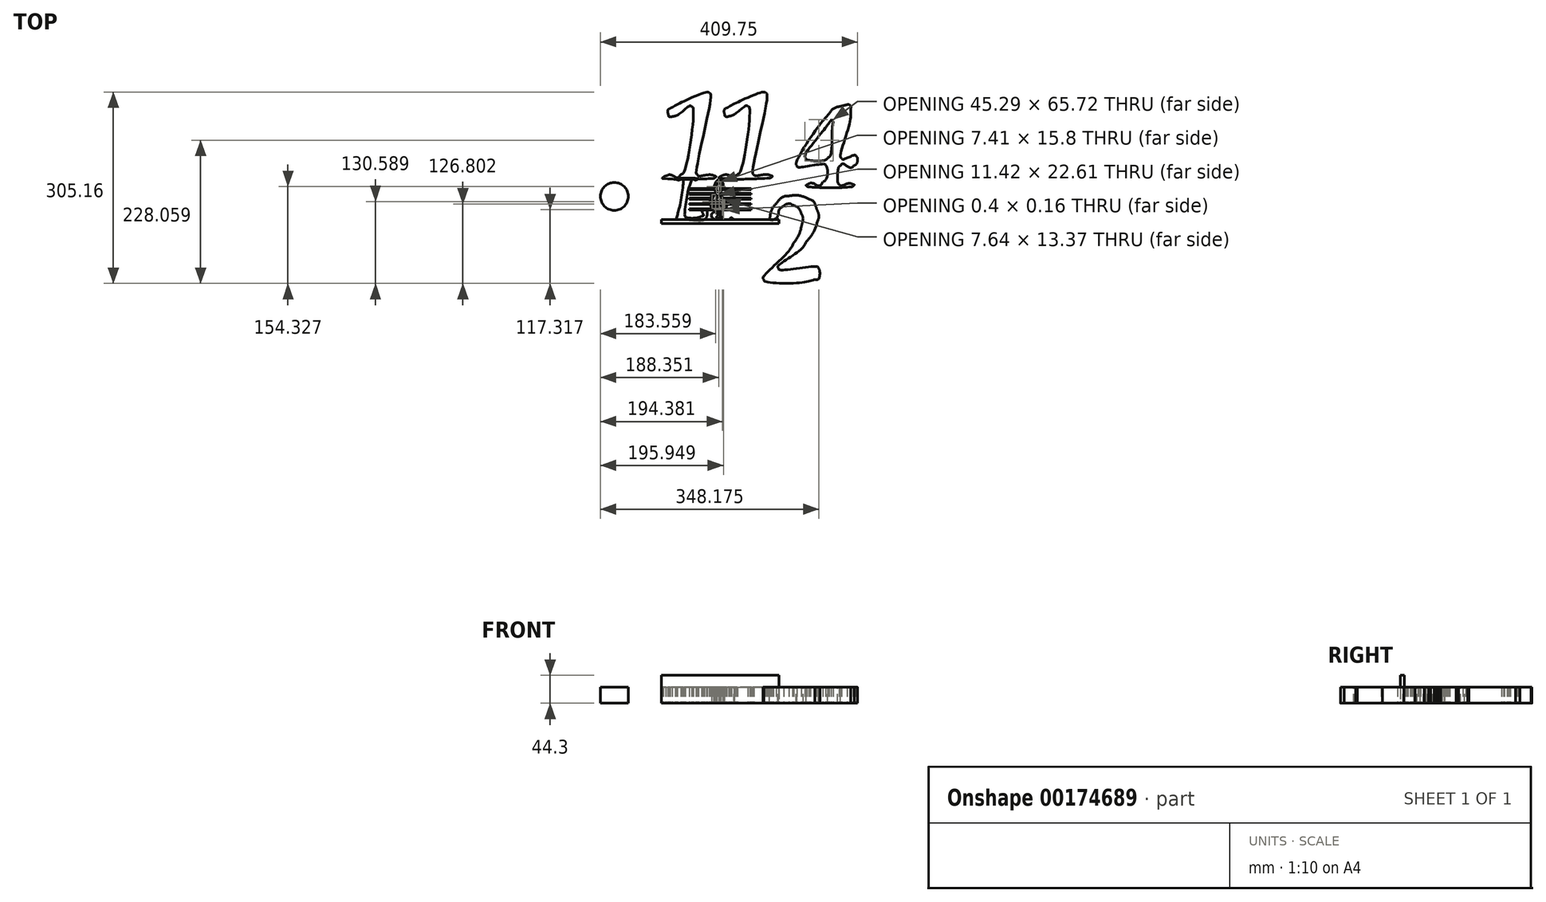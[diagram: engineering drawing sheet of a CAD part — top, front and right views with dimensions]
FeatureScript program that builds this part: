
annotation { "Feature Type Name" : "Feature", "Feature Type Description" : "" }
export const myFeature = defineFeature(function(context is Context, id is Id, definition is map)
    precondition{}
    {
        {
            var Q0;
            Q0=qCreatedBy(makeId("Top.planeOp"),FACE);
            var sketch = newSketch(context, id + "F0", { "sketchPlane" : qUnion([Q0])});
            skFitSpline(sketch, "E0", {"points": [v(-67.19, 65.64) * mm, v(-68.14, 65.58) * mm, v(-66.1, 63.8) * mm, v(-65.16, 63.61) * mm]});
            skFitSpline(sketch, "E1", {"points": [v(-65.16, 63.61) * mm, v(-62.39, 63.08) * mm, v(-57.66, 64.74) * mm, v(-56.7, 63.61) * mm]});
            skFitSpline(sketch, "E2", {"points": [v(-56.7, 63.61) * mm, v(-55.74, 62.49) * mm, v(-61.1, 22.51) * mm, v(-66.5, 2.65) * mm]});
            skFitSpline(sketch, "E3", {"points": [v(-66.5, 2.65) * mm, v(-67.1, 0.47) * mm, v(-71.2, 3.54) * mm, v(-73.28, 2.65) * mm]});
            skFitSpline(sketch, "E4", {"points": [v(-73.28, 2.65) * mm, v(-74.16, 2.28) * mm, v(-72.2, 0.66) * mm, v(-71.25, 0.62) * mm]});
            skFitSpline(sketch, "E5", {"points": [v(-71.25, 0.62) * mm, v(-54.74, -0.03) * mm, v(-24.37, -1.55) * mm, v(-21.68, 0.62) * mm]});
            skFitSpline(sketch, "E6", {"points": [v(-21.68, 0.62) * mm, v(-19, 2.8) * mm, v(-17.38, 14.81) * mm, v(-18.42, 15.86) * mm]});
            skFitSpline(sketch, "E7", {"points": [v(-18.42, 15.86) * mm, v(-19.46, 16.91) * mm, v(-22.45, 16.22) * mm, v(-23.5, 14.84) * mm]});
            skFitSpline(sketch, "E8", {"points": [v(-23.5, 14.84) * mm, v(-25.4, 12.34) * mm, v(-23.13, 6.82) * mm, v(-26.1, 5.76) * mm]});
            skFitSpline(sketch, "E9", {"points": [v(-26.1, 5.76) * mm, v(-34.27, 2.85) * mm, v(-51.14, 3.53) * mm, v(-52.12, 4.63) * mm]});
            skFitSpline(sketch, "E10", {"points": [v(-52.12, 4.63) * mm, v(-53.1, 5.74) * mm, v(-48.12, 44.5) * mm, v(-42.47, 63.61) * mm]});
            skFitSpline(sketch, "E11", {"points": [v(-42.47, 63.61) * mm, v(-41.73, 66.1) * mm, v(-37.22, 63.09) * mm, v(-34.68, 63.61) * mm]});
            skFitSpline(sketch, "E12", {"points": [v(-34.68, 63.61) * mm, v(-33.74, 63.8) * mm, v(-31.69, 65.58) * mm, v(-32.64, 65.64) * mm]});
            skFitSpline(sketch, "E13", {"points": [v(-32.64, 65.64) * mm, v(-44.14, 66.36) * mm, v(-55.7, 66.36) * mm, v(-67.19, 65.64) * mm]});
            skFitSpline(sketch, "E14", {"points": [v(26.27, 65.22) * mm, v(25.32, 65.16) * mm, v(27.37, 63.37) * mm, v(28.3, 63.19) * mm]});
            skFitSpline(sketch, "E15", {"points": [v(28.3, 63.19) * mm, v(31.07, 62.65) * mm, v(35.8, 64.31) * mm, v(36.76, 63.19) * mm]});
            skFitSpline(sketch, "E16", {"points": [v(36.76, 63.19) * mm, v(37.72, 62.07) * mm, v(32.67, 22) * mm, v(26.96, 2.23) * mm]});
            skFitSpline(sketch, "E17", {"points": [v(26.96, 2.23) * mm, v(26.24, -0.27) * mm, v(21.62, 3.1) * mm, v(19.16, 2.23) * mm]});
            skFitSpline(sketch, "E18", {"points": [v(19.16, 2.23) * mm, v(18.26, 1.91) * mm, v(20.24, 0.23) * mm, v(21.2, 0.2) * mm]});
            skFitSpline(sketch, "E19", {"points": [v(21.2, 0.2) * mm, v(38.04, -0.45) * mm, v(69.09, -1.98) * mm, v(71.78, 0.2) * mm]});
            skFitSpline(sketch, "E20", {"points": [v(71.78, 0.2) * mm, v(74.47, 2.37) * mm, v(76.08, 14.39) * mm, v(75.04, 15.44) * mm]});
            skFitSpline(sketch, "E21", {"points": [v(75.04, 15.44) * mm, v(74, 16.49) * mm, v(71, 15.8) * mm, v(69.96, 14.42) * mm]});
            skFitSpline(sketch, "E22", {"points": [v(69.96, 14.42) * mm, v(68.06, 11.91) * mm, v(70.33, 6.4) * mm, v(67.37, 5.34) * mm]});
            skFitSpline(sketch, "E23", {"points": [v(67.37, 5.34) * mm, v(59.19, 2.42) * mm, v(42.32, 3.1) * mm, v(41.34, 4.2) * mm]});
            skFitSpline(sketch, "E24", {"points": [v(41.34, 4.2) * mm, v(40.36, 5.31) * mm, v(45.34, 44.09) * mm, v(51, 63.19) * mm]});
            skFitSpline(sketch, "E25", {"points": [v(51, 63.19) * mm, v(51.73, 65.68) * mm, v(56.24, 62.66) * mm, v(58.79, 63.19) * mm]});
            skFitSpline(sketch, "E26", {"points": [v(58.79, 63.19) * mm, v(59.72, 63.38) * mm, v(61.77, 65.16) * mm, v(60.82, 65.22) * mm]});
            skFitSpline(sketch, "E27", {"points": [v(60.82, 65.22) * mm, v(49.33, 65.94) * mm, v(37.77, 65.94) * mm, v(26.27, 65.22) * mm]});
            skFitSpline(sketch, "E28", {"points": [v(-21.1, 68.31) * mm, v(-18.95, 68.64) * mm, v(-16.7, 68.16) * mm, v(-14.64, 67.5) * mm]});
            skFitSpline(sketch, "E29", {"points": [v(-14.64, 67.5) * mm, v(-12.7, 66.88) * mm, v(-10.84, 65.85) * mm, v(-9.27, 64.55) * mm]});
            skFitSpline(sketch, "E30", {"points": [v(-9.27, 64.55) * mm, v(-7.12, 62.77) * mm, v(-5.25, 60.63) * mm, v(-3.62, 58.37) * mm]});
            skFitSpline(sketch, "E31", {"points": [v(-3.62, 58.37) * mm, v(-2.27, 56.48) * mm, v(-0.79, 52.19) * mm, v(-0.4, 52.18) * mm]});
            skFitSpline(sketch, "E32", {"points": [v(-0.4, 52.18) * mm, v(0, 52.18) * mm, v(2.03, 57.19) * mm, v(3.64, 59.44) * mm]});
            skFitSpline(sketch, "E33", {"points": [v(3.64, 59.44) * mm, v(4.92, 61.25) * mm, v(6.51, 62.84) * mm, v(8.2, 64.28) * mm]});
            skFitSpline(sketch, "E34", {"points": [v(8.2, 64.28) * mm, v(9.5, 65.37) * mm, v(10.95, 66.32) * mm, v(12.5, 66.97) * mm]});
            skFitSpline(sketch, "E35", {"points": [v(12.5, 66.97) * mm, v(14.21, 67.68) * mm, v(16.04, 68.17) * mm, v(17.88, 68.31) * mm]});
            skFitSpline(sketch, "E36", {"points": [v(17.88, 68.31) * mm, v(21.33, 68.58) * mm, v(25.13, 67.5) * mm, v(27.83, 65.35) * mm]});
            skFitSpline(sketch, "E37", {"points": [v(27.83, 65.35) * mm, v(29.52, 64.01) * mm, v(31.1, 62.41) * mm, v(32.13, 60.52) * mm]});
            skFitSpline(sketch, "E38", {"points": [v(32.13, 60.52) * mm, v(33.57, 57.85) * mm, v(34.71, 54.92) * mm, v(35.09, 51.91) * mm]});
            skFitSpline(sketch, "E39", {"points": [v(35.09, 51.91) * mm, v(35.86, 45.7) * mm, v(34.5, 39.2) * mm, v(32.13, 33.37) * mm]});
            skFitSpline(sketch, "E40", {"points": [v(32.13, 33.37) * mm, v(31, 30.58) * mm, v(29.63, 27.89) * mm, v(28.1, 25.3) * mm]});
            skFitSpline(sketch, "E41", {"points": [v(28.1, 25.3) * mm, v(26.76, 23.03) * mm, v(25.23, 20.86) * mm, v(23.53, 18.85) * mm]});
            skFitSpline(sketch, "E42", {"points": [v(23.53, 18.85) * mm, v(21.2, 16.1) * mm, v(18.67, 13.48) * mm, v(16, 11.05) * mm]});
            skFitSpline(sketch, "E43", {"points": [v(16, 11.05) * mm, v(13.73, 9) * mm, v(11.3, 7.1) * mm, v(8.74, 5.4) * mm]});
            skFitSpline(sketch, "E44", {"points": [v(8.74, 5.4) * mm, v(5.9, 3.52) * mm, v(1.61, 0.32) * mm, v(-0.13, 0.3) * mm]});
            skFitSpline(sketch, "E45", {"points": [v(-0.13, 0.3) * mm, v(-1.87, 0.29) * mm, v(-7.2, 3.64) * mm, v(-10.34, 5.95) * mm]});
            skFitSpline(sketch, "E46", {"points": [v(-10.34, 5.95) * mm, v(-14.69, 9.14) * mm, v(-18.7, 12.8) * mm, v(-22.44, 16.7) * mm]});
            skFitSpline(sketch, "E47", {"points": [v(-22.44, 16.7) * mm, v(-24.92, 19.29) * mm, v(-27.1, 22.2) * mm, v(-28.9, 25.3) * mm]});
            skFitSpline(sketch, "E48", {"points": [v(-28.9, 25.3) * mm, v(-31.06, 29.05) * mm, v(-32.8, 33.06) * mm, v(-34.27, 37.13) * mm]});
            skFitSpline(sketch, "E49", {"points": [v(-34.27, 37.13) * mm, v(-35.14, 39.54) * mm, v(-35.6, 42.1) * mm, v(-35.88, 44.66) * mm]});
            skFitSpline(sketch, "E50", {"points": [v(-35.88, 44.66) * mm, v(-36.35, 48.86) * mm, v(-36.04, 53.38) * mm, v(-34.54, 57.3) * mm]});
            skFitSpline(sketch, "E51", {"points": [v(-34.54, 57.3) * mm, v(-33.87, 59.01) * mm, v(-32.94, 60.64) * mm, v(-31.85, 62.13) * mm]});
            skFitSpline(sketch, "E52", {"points": [v(-31.85, 62.13) * mm, v(-30.95, 63.36) * mm, v(-29.94, 64.6) * mm, v(-28.62, 65.35) * mm]});
            skFitSpline(sketch, "E53", {"points": [v(-28.62, 65.35) * mm, v(-26.28, 66.7) * mm, v(-23.76, 67.9) * mm, v(-21.1, 68.31) * mm]});
            skPoint(sketch, "E54", {"position": v(-0.13, 0.3) * mm});
            skSolve(sketch);
        }
        {
            var Q0;
            Q0=qCreatedBy(makeId("Top.planeOp"),FACE);
            var sketch = newSketch(context, id + "F1", { "sketchPlane" : qUnion([Q0])});
            skFitSpline(sketch, "E55", {"points": [v(-13.96, 201.4) * mm, v(-16.25, 203.24) * mm, v(-56.77, 187.9) * mm, v(-76.45, 177.37) * mm]});
            skFitSpline(sketch, "E56", {"points": [v(-76.45, 177.37) * mm, v(-79.73, 175.62) * mm, v(-80.1, 170.16) * mm, v(-79.16, 166.56) * mm]});
            skFitSpline(sketch, "E57", {"points": [v(-79.16, 166.56) * mm, v(-78.62, 164.5) * mm, v(-75.1, 163.82) * mm, v(-73.1, 164.55) * mm]});
            skFitSpline(sketch, "E58", {"points": [v(-73.1, 164.55) * mm, v(-62.33, 168.46) * mm, v(-44.7, 181.66) * mm, v(-42.34, 179.93) * mm]});
            skFitSpline(sketch, "E59", {"points": [v(-42.34, 179.93) * mm, v(-39.98, 178.2) * mm, v(-53.95, 77.46) * mm, v(-59.58, 72.15) * mm]});
            skFitSpline(sketch, "E60", {"points": [v(-59.58, 72.15) * mm, v(-65.22, 66.84) * mm, v(-75.48, 71.57) * mm, v(-83.19, 69.79) * mm]});
            skFitSpline(sketch, "E61", {"points": [v(-83.19, 69.79) * mm, v(-85.04, 69.36) * mm, v(-89.12, 65.86) * mm, v(-87.22, 65.76) * mm]});
            skFitSpline(sketch, "E62", {"points": [v(-87.22, 65.76) * mm, v(-61.05, 64.34) * mm, v(-34.77, 64.58) * mm, v(-8.6, 65.76) * mm]});
            skFitSpline(sketch, "E63", {"points": [v(-8.6, 65.76) * mm, v(-6.85, 65.83) * mm, v(-3.2, 69.02) * mm, v(-4.9, 69.45) * mm]});
            skFitSpline(sketch, "E64", {"points": [v(-4.9, 69.45) * mm, v(-14.03, 71.79) * mm, v(-31.24, 69.71) * mm, v(-33.05, 72.01) * mm]});
            skFitSpline(sketch, "E65", {"points": [v(-33.05, 72.01) * mm, v(-34.86, 74.31) * mm, v(-11.68, 199.58) * mm, v(-13.96, 201.4) * mm]});
            skFitSpline(sketch, "E66", {"points": [v(75.76, 201.83) * mm, v(73.47, 203.66) * mm, v(32.95, 188.31) * mm, v(13.26, 177.8) * mm]});
            skFitSpline(sketch, "E67", {"points": [v(13.26, 177.8) * mm, v(9.99, 176.04) * mm, v(9.62, 170.58) * mm, v(10.56, 166.98) * mm]});
            skFitSpline(sketch, "E68", {"points": [v(10.56, 166.98) * mm, v(11.1, 164.93) * mm, v(14.61, 164.24) * mm, v(16.6, 164.97) * mm]});
            skFitSpline(sketch, "E69", {"points": [v(16.6, 164.97) * mm, v(27.39, 168.88) * mm, v(45.02, 182.08) * mm, v(47.38, 180.35) * mm]});
            skFitSpline(sketch, "E70", {"points": [v(47.38, 180.35) * mm, v(49.74, 178.62) * mm, v(35.77, 77.88) * mm, v(30.13, 72.57) * mm]});
            skFitSpline(sketch, "E71", {"points": [v(30.13, 72.57) * mm, v(24.5, 67.26) * mm, v(14.23, 72) * mm, v(6.53, 70.2) * mm]});
            skFitSpline(sketch, "E72", {"points": [v(6.53, 70.2) * mm, v(4.68, 69.78) * mm, v(0.6, 66.28) * mm, v(2.5, 66.18) * mm]});
            skFitSpline(sketch, "E73", {"points": [v(2.5, 66.18) * mm, v(28.67, 64.76) * mm, v(54.94, 65) * mm, v(81.13, 66.18) * mm]});
            skFitSpline(sketch, "E74", {"points": [v(81.13, 66.18) * mm, v(82.87, 66.25) * mm, v(86.5, 69.44) * mm, v(84.82, 69.87) * mm]});
            skFitSpline(sketch, "E75", {"points": [v(84.82, 69.87) * mm, v(75.7, 72.2) * mm, v(58.48, 70.13) * mm, v(56.66, 72.43) * mm]});
            skFitSpline(sketch, "E76", {"points": [v(56.66, 72.43) * mm, v(54.85, 74.73) * mm, v(78.04, 200) * mm, v(75.76, 201.83) * mm]});
            skFitSpline(sketch, "E77", {"points": [v(205.18, 183.26) * mm, v(207.95, 183.9) * mm, v(211.5, 180.05) * mm, v(211.22, 177.2) * mm]});
            skFitSpline(sketch, "E78", {"points": [v(211.22, 177.2) * mm, v(208.57, 150.6) * mm, v(194.7, 100.45) * mm, v(196.69, 98.3) * mm]});
            skFitSpline(sketch, "E79", {"points": [v(196.69, 98.3) * mm, v(198.68, 96.17) * mm, v(217.94, 103.09) * mm, v(219.86, 100.88) * mm]});
            skFitSpline(sketch, "E80", {"points": [v(219.86, 100.88) * mm, v(221.8, 98.68) * mm, v(220.54, 88.98) * mm, v(216.26, 86.48) * mm]});
            skFitSpline(sketch, "E81", {"points": [v(216.26, 86.48) * mm, v(210.22, 82.95) * mm, v(198.45, 89.44) * mm, v(195.25, 86.48) * mm]});
            skFitSpline(sketch, "E82", {"points": [v(195.25, 86.48) * mm, v(192.05, 83.52) * mm, v(190.93, 58.39) * mm, v(192.92, 56.24) * mm]});
            skFitSpline(sketch, "E83", {"points": [v(192.92, 56.24) * mm, v(194.91, 54.1) * mm, v(207.99, 57.84) * mm, v(215.26, 56.24) * mm]});
            skFitSpline(sketch, "E84", {"points": [v(215.26, 56.24) * mm, v(217.11, 55.83) * mm, v(213.12, 52.32) * mm, v(211.22, 52.2) * mm]});
            skFitSpline(sketch, "E85", {"points": [v(211.22, 52.2) * mm, v(189.08, 50.94) * mm, v(166.84, 51.13) * mm, v(144.7, 52.2) * mm]});
            skFitSpline(sketch, "E86", {"points": [v(144.7, 52.2) * mm, v(143.09, 52.29) * mm, v(139.77, 55.07) * mm, v(141.28, 55.62) * mm]});
            skFitSpline(sketch, "E87", {"points": [v(141.28, 55.62) * mm, v(149.43, 58.58) * mm, v(160.83, 54.05) * mm, v(166.87, 60.27) * mm]});
            skFitSpline(sketch, "E88", {"points": [v(166.87, 60.27) * mm, v(173.04, 66.63) * mm, v(173.13, 84.25) * mm, v(171.24, 86.48) * mm]});
            skFitSpline(sketch, "E89", {"points": [v(171.24, 86.48) * mm, v(169.35, 88.72) * mm, v(126.7, 83.92) * mm, v(125.29, 86.48) * mm]});
            skFitSpline(sketch, "E90", {"points": [v(125.29, 86.48) * mm, v(123.87, 89.04) * mm, v(156.26, 144.09) * mm, v(176.95, 169.14) * mm]});
            skFitSpline(sketch, "E91", {"points": [v(176.95, 169.14) * mm, v(183.65, 177.26) * mm, v(194.94, 180.85) * mm, v(205.18, 183.26) * mm]});
            skFitSpline(sketch, "E92", {"points": [v(179.78, 158.25) * mm, v(180.7, 159.45) * mm, v(183.13, 156.54) * mm, v(183, 155.03) * mm]});
            skFitSpline(sketch, "E93", {"points": [v(183, 155.03) * mm, v(181.36, 136.08) * mm, v(178.93, 102.28) * mm, v(174.64, 98.58) * mm]});
            skFitSpline(sketch, "E94", {"points": [v(174.64, 98.58) * mm, v(170.34, 94.88) * mm, v(140.66, 96) * mm, v(139.3, 98.58) * mm]});
            skFitSpline(sketch, "E95", {"points": [v(139.3, 98.58) * mm, v(137.92, 101.17) * mm, v(165.07, 139.24) * mm, v(179.78, 158.25) * mm]});
            skCircle(sketch, "E96", {"center": v(-165.43, 37.15) * mm, "radius": 22.2 * mm});
            skCircle(sketch, "E97", {"center": v(-179.1, -33.64) * mm, "radius": 24.93 * mm});
            skFitSpline(sketch, "E98", {"points": [v(-168.77, 68.16) * mm, v(-157.86, 69) * mm, v(-145.47, 68.38) * mm, v(-136.51, 62.1) * mm]});
            skFitSpline(sketch, "E99", {"points": [v(-136.51, 62.1) * mm, v(-130.07, 57.6) * mm, v(-128.88, 47.79) * mm, v(-128.45, 39.93) * mm]});
            skFitSpline(sketch, "E100", {"points": [v(-128.45, 39.93) * mm, v(-128.16, 34.82) * mm, v(-131.13, 29.67) * mm, v(-134.5, 25.82) * mm]});
            skFitSpline(sketch, "E101", {"points": [v(-134.5, 25.82) * mm, v(-140.79, 18.63) * mm, v(-156.7, 10.6) * mm, v(-156.67, 7.67) * mm]});
            skFitSpline(sketch, "E102", {"points": [v(-156.67, 7.67) * mm, v(-156.64, 4.75) * mm, v(-142.22, 0.28) * mm, v(-138.53, -6.44) * mm]});
            skFitSpline(sketch, "E103", {"points": [v(-138.53, -6.44) * mm, v(-134.27, -14.18) * mm, v(-132.35, -24.07) * mm, v(-134.5, -32.65) * mm]});
            skFitSpline(sketch, "E104", {"points": [v(-134.5, -32.65) * mm, v(-136.71, -41.52) * mm, v(-143.66, -48.9) * mm, v(-150.63, -54.83) * mm]});
            skFitSpline(sketch, "E105", {"points": [v(-150.63, -54.83) * mm, v(-157.5, -60.66) * mm, v(-165.9, -65.6) * mm, v(-174.82, -66.92) * mm]});
            skFitSpline(sketch, "E106", {"points": [v(-174.82, -66.92) * mm, v(-184.88, -68.41) * mm, v(-195.46, -66.25) * mm, v(-205.06, -62.9) * mm]});
            skFitSpline(sketch, "E107", {"points": [v(-205.06, -62.9) * mm, v(-209.55, -61.32) * mm, v(-213.56, -57.3) * mm, v(-215.14, -52.8) * mm]});
            skFitSpline(sketch, "E108", {"points": [v(-215.14, -52.8) * mm, v(-217.83, -45.18) * mm, v(-221, -35.74) * mm, v(-217.16, -28.62) * mm]});
            skFitSpline(sketch, "E109", {"points": [v(-217.16, -28.62) * mm, v(-210.62, -16.47) * mm, v(-186.97, -3.32) * mm, v(-186.92, -0.4) * mm]});
            skFitSpline(sketch, "E110", {"points": [v(-186.92, -0.4) * mm, v(-186.86, 2.54) * mm, v(-200.22, 8.68) * mm, v(-203.04, 15.74) * mm]});
            skFitSpline(sketch, "E111", {"points": [v(-203.04, 15.74) * mm, v(-206.04, 23.23) * mm, v(-205.6, 32.28) * mm, v(-203.04, 39.93) * mm]});
            skFitSpline(sketch, "E112", {"points": [v(-203.04, 39.93) * mm, v(-200.62, 47.2) * mm, v(-194.85, 53.2) * mm, v(-188.93, 58.08) * mm]});
            skFitSpline(sketch, "E113", {"points": [v(-188.93, 58.08) * mm, v(-183.13, 62.85) * mm, v(-176.26, 67.58) * mm, v(-168.77, 68.16) * mm]});
            skFitSpline(sketch, "E114", {"points": [v(112.48, 37.8) * mm, v(124, 39.09) * mm, v(136.2, 36.56) * mm, v(146.75, 31.76) * mm]});
            skFitSpline(sketch, "E115", {"points": [v(146.75, 31.76) * mm, v(152.01, 29.37) * mm, v(154.8, 23.06) * mm, v(156.83, 17.65) * mm]});
            skFitSpline(sketch, "E116", {"points": [v(156.83, 17.65) * mm, v(158.97, 11.95) * mm, v(160.64, 5.32) * mm, v(158.85, -0.5) * mm]});
            skFitSpline(sketch, "E117", {"points": [v(158.85, -0.5) * mm, v(155.05, -12.85) * mm, v(148.88, -24.76) * mm, v(140.7, -34.77) * mm]});
            skFitSpline(sketch, "E118", {"points": [v(140.7, -34.77) * mm, v(127.76, -50.62) * mm, v(95.16, -74.4) * mm, v(96.25, -77.11) * mm]});
            skFitSpline(sketch, "E119", {"points": [v(96.25, -77.11) * mm, v(97.34, -79.83) * mm, v(157.66, -74.77) * mm, v(159.42, -77.11) * mm]});
            skFitSpline(sketch, "E120", {"points": [v(159.42, -77.11) * mm, v(161.19, -79.45) * mm, v(160.4, -93.97) * mm, v(154.24, -95.26) * mm]});
            skFitSpline(sketch, "E121", {"points": [v(154.24, -95.26) * mm, v(127.57, -100.82) * mm, v(73.77, -97.9) * mm, v(72.52, -95.26) * mm]});
            skFitSpline(sketch, "E122", {"points": [v(72.52, -95.26) * mm, v(71.26, -92.6) * mm, v(105.94, -57.35) * mm, v(120.54, -36.79) * mm]});
            skFitSpline(sketch, "E123", {"points": [v(120.54, -36.79) * mm, v(126.11, -28.94) * mm, v(130.21, -19.89) * mm, v(132.64, -10.58) * mm]});
            skFitSpline(sketch, "E124", {"points": [v(132.64, -10.58) * mm, v(134.34, -4.08) * mm, v(135.2, 3.37) * mm, v(132.64, 9.58) * mm]});
            skFitSpline(sketch, "E125", {"points": [v(132.64, 9.58) * mm, v(130.1, 15.73) * mm, v(124.64, 21.07) * mm, v(118.53, 23.7) * mm]});
            skFitSpline(sketch, "E126", {"points": [v(118.53, 23.7) * mm, v(114.16, 25.57) * mm, v(108.12, 24.65) * mm, v(104.41, 21.68) * mm]});
            skFitSpline(sketch, "E127", {"points": [v(104.41, 21.68) * mm, v(97.28, 15.97) * mm, v(95.05, 5.65) * mm, v(88.28, -0.5) * mm]});
            skFitSpline(sketch, "E128", {"points": [v(88.28, -0.5) * mm, v(86.71, -1.93) * mm, v(81.91, -0.58) * mm, v(82.24, 1.52) * mm]});
            skFitSpline(sketch, "E129", {"points": [v(82.24, 1.52) * mm, v(83.56, 10.15) * mm, v(86.72, 19) * mm, v(92.32, 25.71) * mm]});
            skFitSpline(sketch, "E130", {"points": [v(92.32, 25.71) * mm, v(97.33, 31.73) * mm, v(104.69, 36.94) * mm, v(112.48, 37.8) * mm]});
            skSolve(sketch);
        }
        {
            var Q0;
            Q0=qCreatedBy(makeId("Front.planeOp"),FACE);
            var sketch = newSketch(context, id + "F2", { "sketchPlane" : qUnion([Q0])});
            skLineSegment(sketch, "E131.bottom", {"start": v(-90.24, 44.3) * mm, "end": v(96.59, 44.3) * mm});
            skLineSegment(sketch, "E131.top", {"start": v(-90.24, 0) * mm, "end": v(96.59, 0) * mm});
            skLineSegment(sketch, "E131.left", {"start": v(-90.24, 44.3) * mm, "end": v(-90.24, 0) * mm});
            skLineSegment(sketch, "E131.right", {"start": v(96.59, 44.3) * mm, "end": v(96.59, 0) * mm});
            skSolve(sketch);
        }
        {
            var Q0;
            Q0=qCreatedBy(makeId("Top.planeOp"),FACE);
            var sketch = newSketch(context, id + "F3", { "sketchPlane" : qUnion([Q0])});
            skFitSpline(sketch, "E132", {"points": [v(-5.3, 47.83) * mm, v(-5.86, 54.73) * mm, v(0.98, 64.25) * mm, v(7.14, 59.17) * mm, v(5.66, 46.69) * mm, v(0, 41.97) * mm], "startDerivative": vector(-5.6, 41.47) * mm, "endDerivative": vector(-39.7, -43.44) * mm});
            skFitSpline(sketch, "E133", {"points": [v(0, 60.06) * mm, v(-2.64, 55.14) * mm, v(-2.9, 49.86) * mm, v(-1.46, 44.95) * mm, v(2.21, 47.64) * mm, v(4.41, 52.36) * mm, v(3.06, 60.64) * mm, v(0, 60.06) * mm]});
            skFitSpline(sketch, "E134", {"points": [v(-5.3, 47.83) * mm, v(-5.3, 43.19) * mm, v(-10.5, 37.81) * mm, v(-12.78, 25.6) * mm, v(-7.85, 15.62) * mm, v(1.82, 14.54) * mm], "startDerivative": vector(32.53, -78.9) * mm, "endDerivative": vector(54.35, 5.43) * mm});
            skFitSpline(sketch, "E135", {"points": [v(-5.6, 38.99) * mm, v(-7.33, 37.3) * mm, v(-9.74, 28.78) * mm, v(-5.98, 19.06) * mm, v(1.6, 18.11) * mm, v(1.43, 19.35) * mm, v(-0.79, 30.61) * mm, v(-3, 29.17) * mm, v(-3.77, 25.51) * mm, v(-2.04, 23.2) * mm, v(-1.56, 20.8) * mm, v(-5.07, 22.67) * mm, v(-5.6, 29.84) * mm, v(-1.65, 34.37) * mm, v(-1.65, 35.62) * mm, v(-2.69, 39.1) * mm, v(-3.2, 40.43) * mm, v(-5.6, 38.99) * mm]});
            skFitSpline(sketch, "E136", {"points": [v(0, 41.97) * mm, v(2.3, 35.59) * mm, v(5.8, 36.08) * mm, v(12.46, 30.82) * mm, v(12.88, 19.68) * mm, v(8.53, 15.92) * mm, v(7.62, 15.66) * mm], "startDerivative": vector(7.56, -39.68) * mm, "endDerivative": vector(-6.64, 1.58) * mm});
            skFitSpline(sketch, "E137", {"points": [v(3.45, 31.57) * mm, v(3.06, 28.5) * mm, v(5.09, 18.87) * mm, v(8.17, 19.83) * mm, v(10.56, 24.3) * mm, v(7.69, 31.25) * mm, v(3.45, 31.57) * mm]});
            skFitSpline(sketch, "E138", {"points": [v(1.82, 14.54) * mm, v(2.47, 10.16) * mm, v(2.87, 3.85) * mm, v(0, 2.7) * mm, v(-3.2, 2.8) * mm, v(-3.2, 3.76) * mm, v(-1.62, 5.08) * mm, v(-0.2, 7.82) * mm, v(-1.84, 10.87) * mm, v(-5.62, 12.24) * mm, v(-9.83, 9.78) * mm, v(-10.86, 6.25) * mm, v(-9.97, 3.87) * mm, v(-6.59, 0.95) * mm, v(0.95, 0) * mm, v(4.5, 1.35) * mm, v(6.34, 5.28) * mm, v(5.44, 14.54) * mm, v(7.77, 15.62) * mm, v(8.53, 15.92) * mm], "startDerivative": vector(8.69, -71.8) * mm, "endDerivative": vector(18.16, 2.08) * mm});
            skPoint(sketch, "E139", {"position": v(-3.85, 32.12) * mm});
            skLineSegment(sketch, "E140.bottom", {"start": v(-45.75, 49.51) * mm, "end": v(52.46, 49.51) * mm});
            skLineSegment(sketch, "E140.top", {"start": v(-45.75, 47.83) * mm, "end": v(52.46, 47.83) * mm});
            skLineSegment(sketch, "E140.left", {"start": v(-45.75, 49.51) * mm, "end": v(-45.75, 47.83) * mm});
            skLineSegment(sketch, "E140.right", {"start": v(52.46, 49.51) * mm, "end": v(52.46, 47.83) * mm});
            skLineSegment(sketch, "E141.bottom", {"start": v(-45.78, 42.21) * mm, "end": v(52.43, 42.21) * mm});
            skLineSegment(sketch, "E141.top", {"start": v(-45.78, 40.53) * mm, "end": v(52.43, 40.53) * mm});
            skLineSegment(sketch, "E141.left", {"start": v(-45.78, 42.21) * mm, "end": v(-45.78, 40.53) * mm});
            skLineSegment(sketch, "E141.right", {"start": v(52.43, 42.21) * mm, "end": v(52.43, 40.53) * mm});
            skLineSegment(sketch, "E142.bottom", {"start": v(-45.8, 34.62) * mm, "end": v(52.42, 34.62) * mm});
            skLineSegment(sketch, "E142.top", {"start": v(-45.8, 32.94) * mm, "end": v(52.42, 32.94) * mm});
            skLineSegment(sketch, "E142.left", {"start": v(-45.8, 34.62) * mm, "end": v(-45.8, 32.94) * mm});
            skLineSegment(sketch, "E142.right", {"start": v(52.42, 34.62) * mm, "end": v(52.42, 32.94) * mm});
            skLineSegment(sketch, "E143.bottom", {"start": v(-45.8, 25.9) * mm, "end": v(52.42, 25.9) * mm});
            skLineSegment(sketch, "E143.top", {"start": v(-45.8, 24.22) * mm, "end": v(52.42, 24.22) * mm});
            skLineSegment(sketch, "E143.left", {"start": v(-45.8, 25.9) * mm, "end": v(-45.8, 24.22) * mm});
            skLineSegment(sketch, "E143.right", {"start": v(52.42, 25.9) * mm, "end": v(52.42, 24.22) * mm});
            skLineSegment(sketch, "E144.bottom", {"start": v(-45.85, 17.43) * mm, "end": v(52.36, 17.43) * mm});
            skLineSegment(sketch, "E144.top", {"start": v(-45.85, 15.75) * mm, "end": v(52.36, 15.75) * mm});
            skLineSegment(sketch, "E144.left", {"start": v(-45.85, 17.43) * mm, "end": v(-45.85, 15.75) * mm});
            skLineSegment(sketch, "E144.right", {"start": v(52.36, 17.43) * mm, "end": v(52.36, 15.75) * mm});
            skSolve(sketch);
        }
        {
            var Q0;
            Q0=makeQuery(id+"F0.imprint","IMPRINT",FACE,{"disambiguationData":[TD([[makeQuery(id+"F0.imprint","IMPRINT",EDGE,{"derivedFrom":sQuery(id+"F0.wireOp",EDGE,"E0")}),1.0]])]});
            var Q1;
            {var subQ10=sQuery(id+"F0.wireOp",EDGE,"E17");Q1=makeQuery(id+"F0.imprint","IMPRINT",FACE,{"disambiguationData":[TD([[makeQuery(id+"F0.imprint","IMPRINT",EDGE,{"derivedFrom":subQ10}),1.0]])]});}
            var Q2;
            {var subQ0=sQuery(id+"F0.wireOp",EDGE,"E14");Q2=makeQuery(id+"F0.imprint","IMPRINT",FACE,{"disambiguationData":[TD([[makeQuery(id+"F0.imprint","IMPRINT",EDGE,{"derivedFrom":subQ0}),1.0]])]});}
            var Q3;
            {var subQ0=sQuery(id+"F0.wireOp",EDGE,"E7");var subQ1=sQuery(id+"F0.wireOp",EDGE,"E6");var subQ2=makeQuery(id+"F0.imprint","INTERSECT",VERTEX,{"derivedFrom":[subQ1,subQ0]});Q3=makeQuery(id+"F0.imprint","IMPRINT",FACE,{"disambiguationData":[TD([[makeQuery(id+"F0.imprint","IMPRINT",EDGE,{"disambiguationData":[TD([[subQ2,1.0]])],"derivedFrom":subQ1}),1.0]])]});}
            extrude(context, id + "F4", {"entities" : qUnion([Q0, Q1, Q2, Q3]), "depth" : 25.4 * mm});
        }
        {
            var Q0;
            Q0=makeQuery(id+"F1.imprint","IMPRINT",FACE,{"disambiguationData":[TD([[makeQuery(id+"F1.imprint","IMPRINT",EDGE,{"derivedFrom":sQuery(id+"F1.wireOp",EDGE,"E55")}),1.0]])]});
            var Q1;
            Q1=makeQuery(id+"F1.imprint","IMPRINT",FACE,{"disambiguationData":[TD([[makeQuery(id+"F1.imprint","IMPRINT",EDGE,{"derivedFrom":sQuery(id+"F1.wireOp",EDGE,"E66")}),1.0]])]});
            var Q2;
            Q2=makeQuery(id+"F1.imprint","IMPRINT",FACE,{"disambiguationData":[TD([[makeQuery(id+"F1.imprint","IMPRINT",EDGE,{"derivedFrom":sQuery(id+"F1.wireOp",EDGE,"E77")}),-1.0]])]});
            var Q3;
            Q3=makeQuery(id+"F1.imprint","IMPRINT",FACE,{"disambiguationData":[TD([[makeQuery(id+"F1.imprint","IMPRINT",EDGE,{"derivedFrom":sQuery(id+"F1.wireOp",EDGE,"E96")}),1.0]])]});
            var Q4;
            Q4=makeQuery(id+"F1.imprint","IMPRINT",FACE,{"disambiguationData":[TD([[makeQuery(id+"F1.imprint","IMPRINT",EDGE,{"derivedFrom":sQuery(id+"F1.wireOp",EDGE,"E114")}),-1.0]])]});
            var Q5;
            Q5=sQuery(id+"F1.wireOp",EDGE,"c7cc00ab-f25f-42a7-9330-9939b61b4846");
            var Q6;
            Q6=sQuery(id+"F1.wireOp",EDGE,"f25bb9a9-3208-4804-8311-45a919a4e9d7");
            var Q7;
            Q7=sQuery(id+"F1.wireOp",EDGE,"843194b1-cb39-4e59-84b3-f443d2b2ed2d");
            var Q8;
            Q8=sQuery(id+"F1.wireOp",EDGE,"fd73b015-e9e2-47a3-8cee-78b48e1bb1c8");
            var Q9;
            Q9=sQuery(id+"F1.wireOp",EDGE,"1f206ff0-db46-4620-826d-d70bbf3d78a3");
            var Q10;
            Q10=sQuery(id+"F1.wireOp",EDGE,"01695f1d-dff9-4f9b-8fe2-ccf91e0bb2d9");
            var Q11;
            Q11=sQuery(id+"F1.wireOp",EDGE,"32f496c9-434c-4a42-a456-453a450ef25a");
            var Q12;
            Q12=sQuery(id+"F1.wireOp",EDGE,"f1e4f423-0778-4f18-887f-b8ced6975a27");
            var Q13;
            Q13=sQuery(id+"F1.wireOp",EDGE,"50f9aca0-c4ca-4987-b3e7-d789c735e512");
            var Q14;
            Q14=sQuery(id+"F1.wireOp",EDGE,"892d63bd-c6f6-4b77-9e03-ff4d23a4ebc5");
            var Q15;
            Q15=sQuery(id+"F1.wireOp",EDGE,"9eea7301-c211-4749-b727-e29ea0ed2ce4");
            var Q16;
            Q16=sQuery(id+"F1.wireOp",EDGE,"90398055-b3c3-411f-ad3e-85c2e70ec0a7");
            var Q17;
            Q17=sQuery(id+"F1.wireOp",EDGE,"6a25daee-9104-4236-8762-4ed708dfe10a");
            var Q18;
            Q18=sQuery(id+"F1.wireOp",EDGE,"9c4817a0-864d-4a76-afd6-0ea0e7f3b45a");
            var Q19;
            Q19=sQuery(id+"F1.wireOp",EDGE,"6609a38f-e891-4cee-82b8-8241b089ebb5");
            var Q20;
            Q20=sQuery(id+"F1.wireOp",EDGE,"e3be049d-917c-41fb-82a8-84bd116318f2");
            var Q21;
            Q21=sQuery(id+"F1.wireOp",EDGE,"39e6c882-b98c-4de5-8e09-77840ac4508f");
            extrude(context, id + "F5", {"entities" : qUnion([Q0, Q1, Q2, Q3, Q4]), "surfaceEntities" : qUnion([Q5, Q6, Q7, Q8, Q9, Q10, Q11, Q12, Q13, Q14, Q15, Q16, Q17, Q18, Q19, Q20, Q21]), "depth" : 25.4 * mm});
        }
        {
            var Q0;
            Q0=makeQuery(id+"F2.imprint","IMPRINT",FACE,{"disambiguationData":[TD([[makeQuery(id+"F2.imprint","IMPRINT",EDGE,{"derivedFrom":sQuery(id+"F2.wireOp",EDGE,"E131.bottom")}),-1.0]])]});
            extrude(context, id + "F6", {"entities" : qUnion([Q0]), "depth" : 6.35 * mm});
        }
        {
            var Q0;
            Q0 = qSketchRegion(id + "F3", true);
            var Q1;
            {var subQ0=sQuery(id+"F3.wireOp",EDGE,"E143.top");var subQ1=sQuery(id+"F3.wireOp",EDGE,"E135");var subQ2=makeQuery(id+"F3.imprint","INTERSECT",VERTEX,{"disambiguationData":[OD(2.0)],"derivedFrom":[subQ1,subQ0]});Q1=makeQuery(id+"F3.imprint","IMPRINT",FACE,{"disambiguationData":[TD([[makeQuery(id+"F3.imprint","IMPRINT",EDGE,{"disambiguationData":[TD([[subQ2,-1.0]])],"derivedFrom":subQ1}),-1.0]])]});}
            var Q2;
            {var subQ0=sQuery(id+"F3.wireOp",EDGE,"E143.bottom");var subQ1=sQuery(id+"F3.wireOp",EDGE,"E135");var subQ2=makeQuery(id+"F3.imprint","INTERSECT",VERTEX,{"disambiguationData":[OD(2.0)],"derivedFrom":[subQ1,subQ0]});Q2=makeQuery(id+"F3.imprint","IMPRINT",FACE,{"disambiguationData":[TD([[makeQuery(id+"F3.imprint","IMPRINT",EDGE,{"disambiguationData":[TD([[subQ2,-1.0]])],"derivedFrom":subQ1}),-1.0]])]});}
            var Q3;
            {var subQ0=sQuery(id+"F3.wireOp",EDGE,"E143.top");var subQ1=sQuery(id+"F3.wireOp",EDGE,"E135");var subQ2=makeQuery(id+"F3.imprint","INTERSECT",VERTEX,{"disambiguationData":[OD(1.0)],"derivedFrom":[subQ1,subQ0]});Q3=makeQuery(id+"F3.imprint","IMPRINT",FACE,{"disambiguationData":[TD([[makeQuery(id+"F3.imprint","IMPRINT",EDGE,{"disambiguationData":[TD([[subQ2,-1.0]])],"derivedFrom":subQ1}),-1.0]])]});}
            extrude(context, id + "F7", {"entities" : qUnion([Q0, Q1, Q2, Q3]), "depth" : 25.4 * mm});
        }
    });
